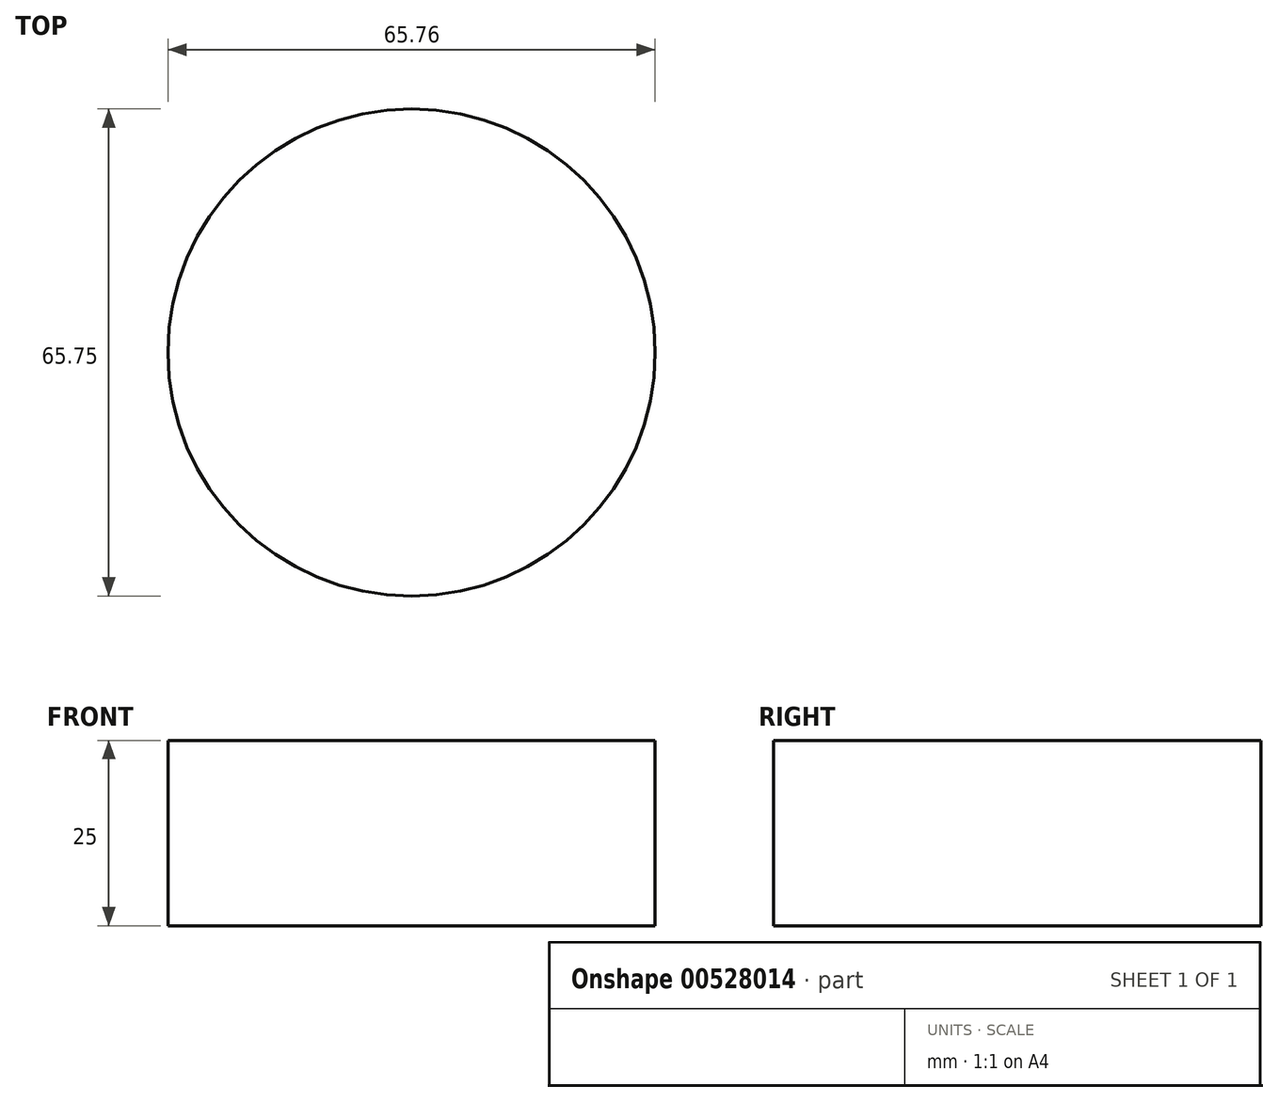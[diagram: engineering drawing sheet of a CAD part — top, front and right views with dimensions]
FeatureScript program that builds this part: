
annotation { "Feature Type Name" : "Feature", "Feature Type Description" : "" }
export const myFeature = defineFeature(function(context is Context, id is Id, definition is map)
    precondition{}
    {
        {
            var Q0;
            Q0=qCreatedBy(makeId("Top.planeOp"),FACE);
            var sketch = newSketch(context, id + "F0", { "sketchPlane" : qUnion([Q0])});
            skCircle(sketch, "E0", {"center": v(0, -0.13) * mm, "radius": 32.88 * mm});
            skSolve(sketch);
        }
        {
            var Q0;
            Q0=makeQuery(id+"F0.imprint","IMPRINT",FACE,{"disambiguationData":[TD([[makeQuery(id+"F0.imprint","IMPRINT",EDGE,{"derivedFrom":sQuery(id+"F0.wireOp",EDGE,"E0")}),1.0]])]});
            extrude(context, id + "F1", {"entities" : qUnion([Q0]), "depth" : 25 * mm, "offsetDistance" : 25 * mm});
        }
    });
